# Revit family: Atdec_ScreenMount_VF-AT
name_source: partatom
category: Specialty Equipment
revit_build: Autodesk Revit 2014
units: mm (PartAtom-declared; Revit-internal decimal feet)

## types (3) — shared parameters
Arm Elevation Max = 360 mm  [stored 1.1811 ft]
Arm Elevation Min = 12 mm  [stored 0.0393701 ft]
Arm Rotation Around Pole = 360°
Assembly Code = E1010800
Category = Desk Mount
Colour Options = Silver, White, Black
Cost = 220 $
Desk Offset = 8 mm  [stored 0.0262467 ft]
Display Pan = 90° left and 90° right
Display Tilt = 70° downward and 70°upward
Green Star Compliant = Yes
Height Adjustable = Yes
Landscape to Portrait Rotaiton = Yes
Manufacturer = Atdec
Manufacturer's Website = http://www.atdec.com.au
Material = Steel, Aluminium, Plastic
Maximum Arm Reach = 413mm
Maximum Desk Thickness = 99mm
Model = VF-AT
Mounting Hole Pattern = 75x75, 100x100
Mounting Options Included = Bolt Through, Desk Clamp
Optional Clamp Type = -
Optional Pole = 590mm
Plastic - Vesa = Plastic - Black
Product Family = Set&Forget
Spring-Assisted = No
Standard Pole Height = 440mm
Supported Weight Range = 0-8kg
URL = http://www.atdec.com.au
Upgradable to Support Additional Arm(s) = Yes
Warranty = 10 Years
zero-valued in all types: Default Elevation

## per-type parameters (varying)
| type | Aluminium | Code | Description | Plastic | Steel |
| Silver - VF-AT | Steel - Silver Polished | VF-AT | Single display desk LCD/LED monitor articulated arm/silver | Plastic - Black | Steel - Black |
| Silver/White - VF-AT-SW | Steel - White | VF-AT-SW | Single display desk LCD/LED monitor articulated arm/silver-white | Plastic - White | Steel - White |
| Black - VF-AT-B | Steel - Black | VF-AT-B | Single display desk LCD/LED monitor articulated arm/black | Plastic - Black | Steel - Black |

note: [stored X ft] marks values corroborated as IEEE doubles in the binary element streams (Revit-internal decimal feet)

## geometry (parser evidence)
native form markers: Sweep x35
no freeform markers — native parametric forms only
